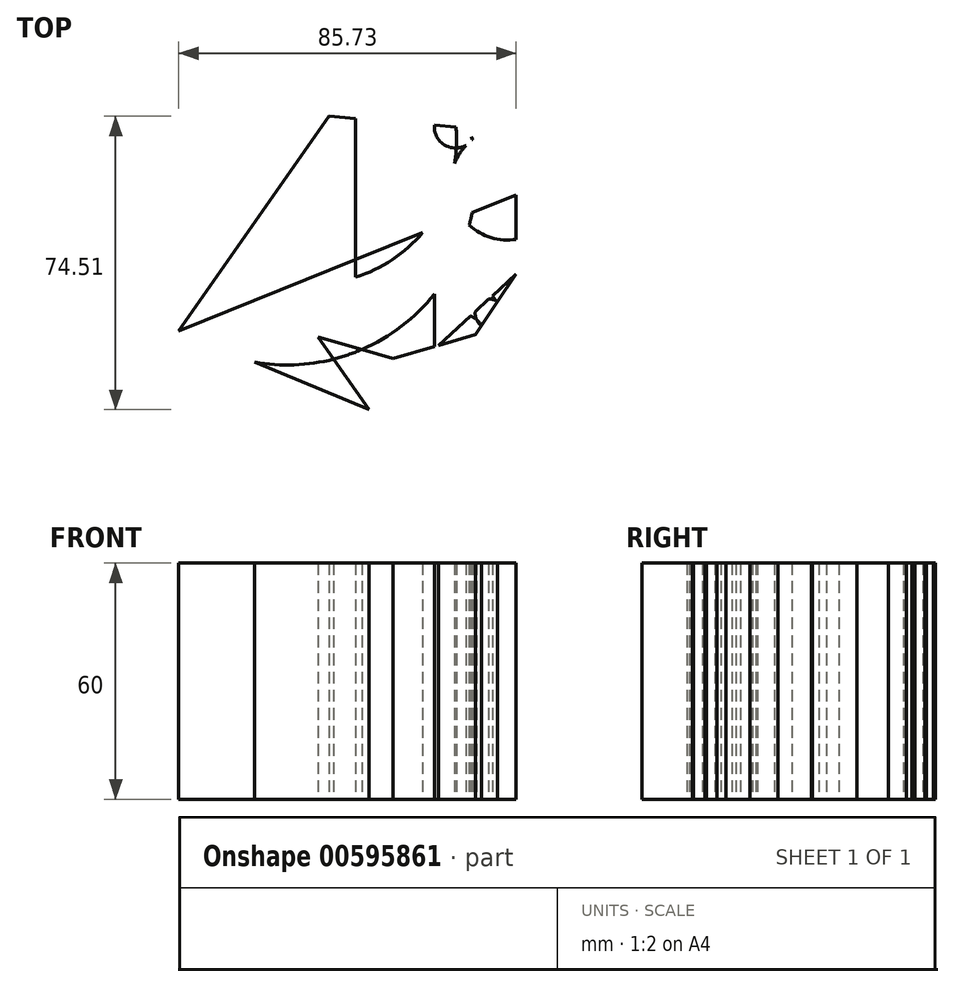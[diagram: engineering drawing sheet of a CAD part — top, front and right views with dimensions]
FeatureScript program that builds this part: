
annotation { "Feature Type Name" : "Feature", "Feature Type Description" : "" }
export const myFeature = defineFeature(function(context is Context, id is Id, definition is map)
    precondition{}
    {
        {
            var Q0;
            Q0=qCreatedBy(makeId("Top.planeOp"),FACE);
            var sketch = newSketch(context, id + "F0", { "sketchPlane" : qUnion([Q0])});
            skLineSegment(sketch, "E0.0", {"start": v(-6.6, -44.84) * mm, "end": v(-54.95, -24.84) * mm});
            skLineSegment(sketch, "E0.1", {"start": v(-54.95, -24.84) * mm, "end": v(-16.75, 29.67) * mm});
            skLineSegment(sketch, "E0.2", {"start": v(-3.27, 28.54) * mm, "end": v(-16.75, 29.67) * mm});
            skLineSegment(sketch, "E0.3", {"start": v(-3.27, 28.54) * mm, "end": v(17.6, 26.78) * mm});
            skLineSegment(sketch, "E0.4", {"start": v(17.6, 26.78) * mm, "end": v(30.77, 9.68) * mm});
            skLineSegment(sketch, "E0.5", {"start": v(30.77, 9.68) * mm, "end": v(30.78, -10.35) * mm});
            skLineSegment(sketch, "E0.6", {"start": v(30.78, -10.35) * mm, "end": v(20.49, -25.8) * mm});
            skLineSegment(sketch, "E0.7", {"start": v(20.49, -25.8) * mm, "end": v(-0.47, -31.86) * mm});
            skLineSegment(sketch, "E0.8", {"start": v(-0.47, -31.86) * mm, "end": v(-19.54, -26.38) * mm});
            skLineSegment(sketch, "E0.9", {"start": v(-6.6, -44.84) * mm, "end": v(-19.54, -26.38) * mm});
            skPoint(sketch, "E0.0.midPoint", {"position": v(-30.78, -34.84) * mm});
            skLineSegment(sketch, "E1", {"start": v(-54.95, -24.84) * mm, "end": v(30.77, 9.68) * mm});
            skLineSegment(sketch, "E2", {"start": v(-6.6, -44.84) * mm, "end": v(30.78, -10.35) * mm});
            skLineSegment(sketch, "E3", {"start": v(-10, 29.1) * mm, "end": v(-10, -29.12) * mm});
            skLineSegment(sketch, "E4", {"start": v(10, 27.42) * mm, "end": v(10, -28.83) * mm});
            skArc(sketch, "E5", {"start": v(-19.54, -26.38) * mm, "mid": v(-13.6, -23.1) * mm, "end": v(-10.3, -29.04) * mm});
            skArc(sketch, "E6", {"start": v(-19.54, -26.38) * mm, "mid": v(-18.28, -19.2) * mm, "end": v(-25.46, -17.93) * mm});
            skArc(sketch, "E7", {"start": v(-25.46, -17.93) * mm, "mid": v(-24.4, -11.92) * mm, "end": v(-30.42, -10.87) * mm});
            skArc(sketch, "E8", {"start": v(-54.95, -24.84) * mm, "mid": v(11.8, -13.1) * mm, "end": v(0.06, 53.65) * mm});
            skArc(sketch, "E9", {"start": v(0.06, 53.65) * mm, "mid": v(-52.59, 5.38) * mm, "end": v(15.5, 26.97) * mm});
            skArc(sketch, "E10", {"start": v(15.5, 26.97) * mm, "mid": v(-10.45, 57.65) * mm, "end": v(-41.13, 31.71) * mm});
            skArc(sketch, "E11", {"start": v(10, 27.42) * mm, "mid": v(13.56, 21.9) * mm, "end": v(19.8, 23.93) * mm});
            skLineSegment(sketch, "E12", {"start": v(19.8, 23.93) * mm, "end": v(19.8, 23.93) * mm});
            skArc(sketch, "E13", {"start": v(19.8, 23.93) * mm, "mid": v(17.19, 3.82) * mm, "end": v(37.3, 1.2) * mm});
            skArc(sketch, "E14", {"start": v(30.78, -10.35) * mm, "mid": v(24.9, -11.53) * mm, "end": v(26.08, -17.4) * mm});
            skArc(sketch, "E15", {"start": v(26.08, -17.4) * mm, "mid": v(20.98, -18.43) * mm, "end": v(22, -23.52) * mm});
            skArc(sketch, "E16", {"start": v(22, -23.52) * mm, "mid": v(13.9, -21.04) * mm, "end": v(10.32, -28.74) * mm});
            skSolve(sketch);
        }
        {
            var Q0;
            {var subQ0=sQuery(id+"F0.wireOp",EDGE,"E3");var subQ1=sQuery(id+"F0.wireOp",EDGE,"E1");var subQ2=makeQuery(id+"F0.imprint","INTERSECT",VERTEX,{"derivedFrom":[subQ1,subQ0]});Q0=makeQuery(id+"F0.imprint","IMPRINT",FACE,{"disambiguationData":[TD([[makeQuery(id+"F0.imprint","IMPRINT",EDGE,{"disambiguationData":[TD([[subQ2,-1.0]])],"derivedFrom":subQ1}),-1.0]])]});}
            var Q1;
            {var subQ0=sQuery(id+"F0.wireOp",EDGE,"E0.0");Q1=makeQuery(id+"F0.imprint","IMPRINT",FACE,{"disambiguationData":[TD([[makeQuery(id+"F0.imprint","IMPRINT",EDGE,{"derivedFrom":subQ0}),-1.0]])]});}
            var Q2;
            {var subQ1=sQuery(id+"F0.wireOp",EDGE,"E0.8");var subQ5=sQuery(id+"F0.wireOp",EDGE,"E0.7");var subQ6=makeQuery(id+"F0.imprint","INTERSECT",VERTEX,{"derivedFrom":[subQ5,subQ1]});Q2=makeQuery(id+"F0.imprint","IMPRINT",FACE,{"disambiguationData":[TD([[makeQuery(id+"F0.imprint","IMPRINT",EDGE,{"disambiguationData":[TD([[subQ6,1.0]])],"derivedFrom":subQ5}),-1.0]])]});}
            var Q3;
            {var subQ1=sQuery(id+"F0.wireOp",EDGE,"E0.2");var subQ7=sQuery(id+"F0.wireOp",EDGE,"E0.3");var subQ8=makeQuery(id+"F0.imprint","INTERSECT",VERTEX,{"derivedFrom":[subQ1,subQ7]});Q3=makeQuery(id+"F0.imprint","IMPRINT",FACE,{"disambiguationData":[TD([[makeQuery(id+"F0.imprint","IMPRINT",EDGE,{"disambiguationData":[TD([[subQ8,1.0]])],"derivedFrom":subQ1}),-1.0]])]});}
            var Q4;
            {var subQ0=sQuery(id+"F0.wireOp",EDGE,"E0.5");Q4=makeQuery(id+"F0.imprint","IMPRINT",FACE,{"disambiguationData":[TD([[makeQuery(id+"F0.imprint","IMPRINT",EDGE,{"derivedFrom":subQ0}),-1.0]])]});}
            extrude(context, id + "F1", {"entities" : qUnion([Q0, Q1, Q2, Q3, Q4]), "depth" : 60 * mm, "offsetDistance" : 25.4 * mm});
        }
        {
            var Q0;
            {var subQ0=sQuery(id+"F0.wireOp",EDGE,"E0.1");Q0=makeQuery(id+"F0.imprint","IMPRINT",FACE,{"disambiguationData":[TD([[makeQuery(id+"F0.imprint","IMPRINT",EDGE,{"derivedFrom":subQ0}),-1.0]])]});}
            var Q1;
            {var subQ0=sQuery(id+"F0.wireOp",EDGE,"E0.4");Q1=makeQuery(id+"F0.imprint","IMPRINT",FACE,{"disambiguationData":[TD([[makeQuery(id+"F0.imprint","IMPRINT",EDGE,{"derivedFrom":subQ0}),-1.0]])]});}
            var Q2;
            {var subQ0=sQuery(id+"F0.wireOp",EDGE,"E0.9");Q2=makeQuery(id+"F0.imprint","IMPRINT",FACE,{"disambiguationData":[TD([[makeQuery(id+"F0.imprint","IMPRINT",EDGE,{"derivedFrom":subQ0}),-1.0]])]});}
            var Q3;
            {var subQ0=sQuery(id+"F0.wireOp",EDGE,"E0.6");Q3=makeQuery(id+"F0.imprint","IMPRINT",FACE,{"disambiguationData":[TD([[makeQuery(id+"F0.imprint","IMPRINT",EDGE,{"derivedFrom":subQ0}),-1.0]])]});}
            var Q4;
            {var subQ0=sQuery(id+"F0.wireOp",EDGE,"E0.7");var subQ1=sQuery(id+"F0.wireOp",EDGE,"E0.6");var subQ2=makeQuery(id+"F0.imprint","INTERSECT",VERTEX,{"derivedFrom":[subQ1,subQ0]});Q4=makeQuery(id+"F0.imprint","IMPRINT",FACE,{"disambiguationData":[TD([[makeQuery(id+"F0.imprint","IMPRINT",EDGE,{"disambiguationData":[TD([[subQ2,-1.0]])],"derivedFrom":subQ0}),-1.0]])]});}
            var Q5;
            {var subQ0=sQuery(id+"F0.wireOp",EDGE,"E12");var subQ1=sQuery(id+"F0.wireOp",EDGE,"E11");var subQ5=makeQuery(id+"F0.imprint","INTERSECT",VERTEX,{"derivedFrom":[subQ1,subQ0]});Q5=makeQuery(id+"F0.imprint","IMPRINT",FACE,{"disambiguationData":[TD([[makeQuery(id+"F0.imprint","IMPRINT",EDGE,{"disambiguationData":[TD([[subQ5,-1.0]])],"derivedFrom":subQ1}),-1.0]])]});}
            var Q6;
            {var subQ0=sQuery(id+"F0.wireOp",EDGE,"E11");var subQ1=sQuery(id+"F0.wireOp",EDGE,"E4");var subQ4=makeQuery(id+"F0.imprint","INTERSECT",VERTEX,{"derivedFrom":[subQ1,subQ0]});Q6=makeQuery(id+"F0.imprint","IMPRINT",FACE,{"disambiguationData":[TD([[makeQuery(id+"F0.imprint","IMPRINT",EDGE,{"disambiguationData":[TD([[subQ4,-1.0]])],"derivedFrom":subQ0}),1.0]])]});}
            var Q7;
            {var subQ0=sQuery(id+"F0.wireOp",EDGE,"E3");var subQ1=sQuery(id+"F0.wireOp",EDGE,"E0.2");var subQ2=makeQuery(id+"F0.imprint","INTERSECT",VERTEX,{"derivedFrom":[subQ1,subQ0]});Q7=makeQuery(id+"F0.imprint","IMPRINT",FACE,{"disambiguationData":[TD([[makeQuery(id+"F0.imprint","IMPRINT",EDGE,{"disambiguationData":[TD([[subQ2,-1.0]])],"derivedFrom":subQ0}),-1.0]])]});}
            var Q8;
            {var subQ0=sQuery(id+"F0.wireOp",EDGE,"E0.2");var subQ1=sQuery(id+"F0.wireOp",EDGE,"E0.1");var subQ2=makeQuery(id+"F0.imprint","INTERSECT",VERTEX,{"derivedFrom":[subQ1,subQ0]});Q8=makeQuery(id+"F0.imprint","IMPRINT",FACE,{"disambiguationData":[TD([[makeQuery(id+"F0.imprint","IMPRINT",EDGE,{"disambiguationData":[TD([[subQ2,1.0]])],"derivedFrom":subQ1}),-1.0]])]});}
            var Q9;
            {var subQ1=sQuery(id+"F0.wireOp",EDGE,"E5");var subQ2=sQuery(id+"F0.wireOp",EDGE,"E0.8");var subQ4=makeQuery(id+"F0.imprint","INTERSECT",VERTEX,{"derivedFrom":[subQ2,subQ1]});Q9=makeQuery(id+"F0.imprint","IMPRINT",FACE,{"disambiguationData":[TD([[makeQuery(id+"F0.imprint","IMPRINT",EDGE,{"disambiguationData":[TD([[subQ4,1.0]])],"derivedFrom":subQ1}),-1.0]])]});}
            var Q10;
            {var subQ0=sQuery(id+"F0.wireOp",EDGE,"E7");var subQ4=sQuery(id+"F0.wireOp",EDGE,"E2");var subQ5=makeQuery(id+"F0.imprint","INTERSECT",VERTEX,{"disambiguationData":[OD(0.0)],"derivedFrom":[subQ4,subQ0]});Q10=makeQuery(id+"F0.imprint","IMPRINT",FACE,{"disambiguationData":[TD([[makeQuery(id+"F0.imprint","IMPRINT",EDGE,{"disambiguationData":[TD([[subQ5,-1.0]])],"derivedFrom":subQ4}),-1.0]])]});}
            extrude(context, id + "F2", {"entities" : qUnion([Q0, Q1, Q2, Q3, Q4, Q5, Q6, Q7, Q8, Q9, Q10]), "depth" : 60 * mm, "offsetDistance" : 25.4 * mm});
        }
    });
